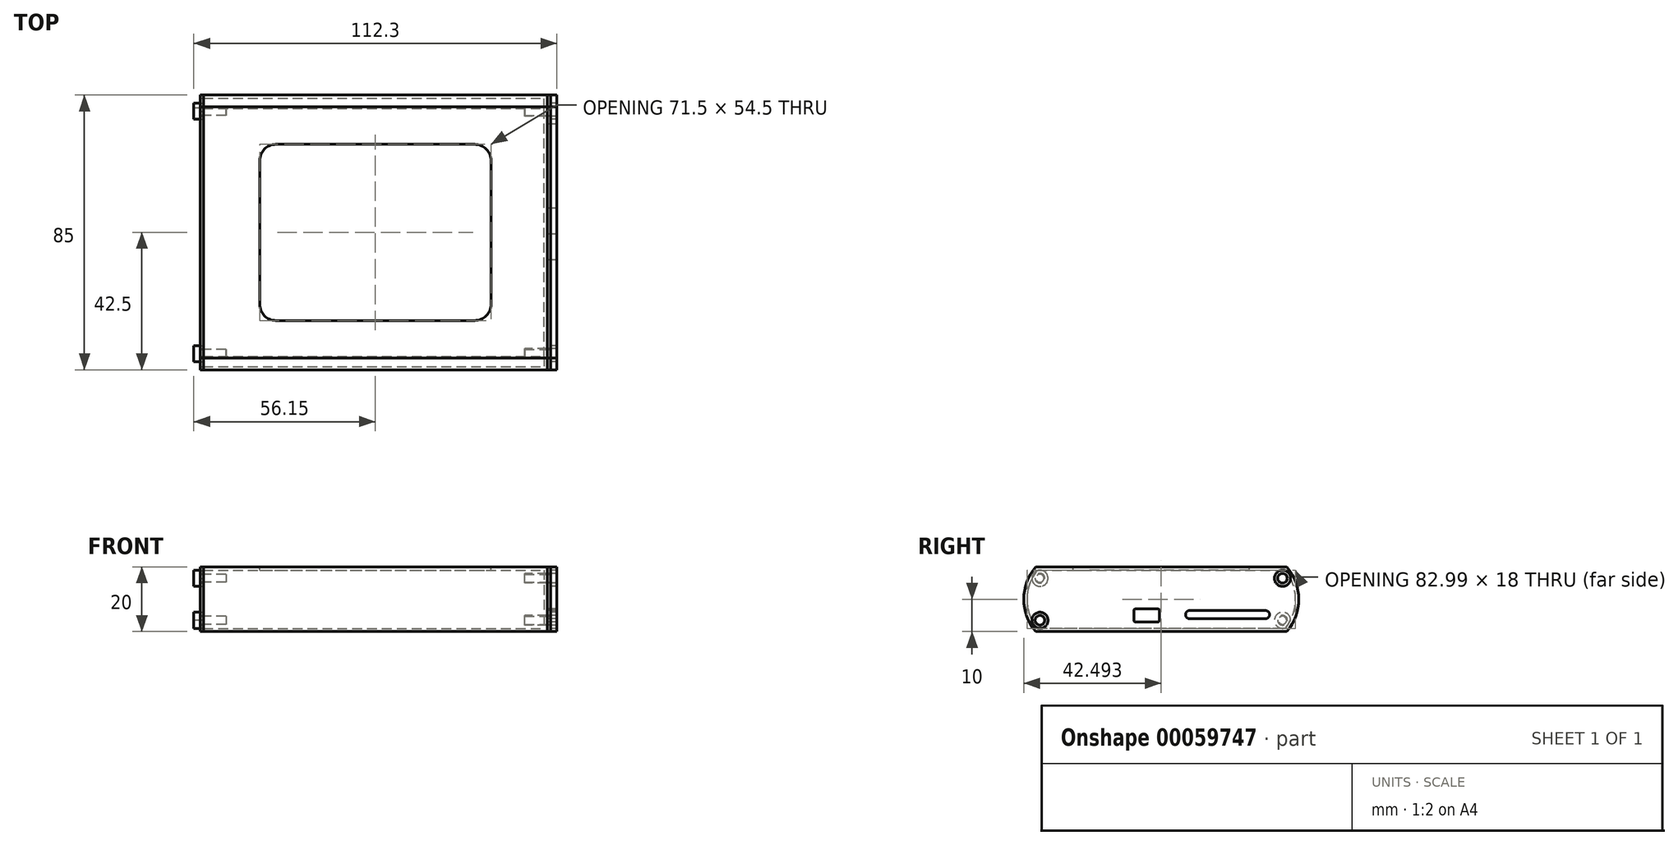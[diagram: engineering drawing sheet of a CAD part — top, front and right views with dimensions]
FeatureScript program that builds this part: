
annotation { "Feature Type Name" : "Feature", "Feature Type Description" : "" }
export const myFeature = defineFeature(function(context is Context, id is Id, definition is map)
    precondition{}
    {
        {
            var Q0;
            Q0=qCreatedBy(makeId("Right.planeOp"),FACE);
            var sketch = newSketch(context, id + "F0", { "sketchPlane" : qUnion([Q0])});
            skLineSegment(sketch, "E0", {"start": v(0, 24.02) * mm, "end": v(0, -24.32) * mm, "construction": true});
            skLineSegment(sketch, "E1", {"start": v(-38.85, 21.54) * mm, "end": v(-38.85, -24.6) * mm, "construction": true});
            skLineSegment(sketch, "E2", {"start": v(-42.5, 19.5) * mm, "end": v(-42.5, -17.74) * mm, "construction": true});
            skLineSegment(sketch, "E3.MirrorCS", {"start": v(38.85, 21.54) * mm, "end": v(38.85, -24.6) * mm, "construction": true});
            skLineSegment(sketch, "E4.MirrorCS", {"start": v(42.5, 19.5) * mm, "end": v(42.5, -17.74) * mm, "construction": true});
            skLineSegment(sketch, "E5", {"start": v(-46.74, 0) * mm, "end": v(47.17, 0) * mm, "construction": true});
            skLineSegment(sketch, "E6", {"start": v(0, 10) * mm, "end": v(-38.85, 10) * mm});
            skLineSegment(sketch, "E7.MirrorCS", {"start": v(0, -10) * mm, "end": v(-38.85, -10) * mm});
            skLineSegment(sketch, "E8.MirrorCS", {"start": v(0, 10) * mm, "end": v(38.85, 10) * mm});
            skLineSegment(sketch, "E9.MirrorCS", {"start": v(0, -10) * mm, "end": v(38.85, -10) * mm});
            skArc(sketch, "E10", {"start": v(-38.85, 10) * mm, "mid": v(-42.5, 0) * mm, "end": v(-38.85, -10) * mm});
            skArc(sketch, "E11.MirrorCS", {"start": v(38.85, 10) * mm, "mid": v(42.5, 0) * mm, "end": v(38.85, -10) * mm});
            skPoint(sketch, "E12.end.orphan", {"position": v(-42.5, 0) * mm});
            skPoint(sketch, "E12.start.orphan", {"position": v(-42.5, 10) * mm});
            skPoint(sketch, "E13.orphan", {"position": v(-42.5, -10) * mm});
            skPoint(sketch, "E14.MirrorCS.end.orphan", {"position": v(42.5, 0) * mm});
            skPoint(sketch, "E14.MirrorCS.start.orphan", {"position": v(42.5, 10) * mm});
            skPoint(sketch, "E15.MirrorCS.start.orphan", {"position": v(42.5, -10) * mm});
            skLineSegment(sketch, "E16", {"start": v(-37.5, 21.54) * mm, "end": v(-37.5, -22.5) * mm, "construction": true});
            skLineSegment(sketch, "E17.MirrorCS", {"start": v(37.5, 21.54) * mm, "end": v(37.5, -22.5) * mm, "construction": true});
            skLineSegment(sketch, "E18", {"start": v(-46, 6.5) * mm, "end": v(47.32, 6.5) * mm, "construction": true});
            skLineSegment(sketch, "E19.MirrorCS", {"start": v(-46, -6.5) * mm, "end": v(47.32, -6.5) * mm, "construction": true});
            skCircle(sketch, "E20", {"center": v(-37.5, 6.5) * mm, "radius": 1.5 * mm});
            skCircle(sketch, "E21.MirrorC", {"center": v(-37.5, -6.5) * mm, "radius": 1.5 * mm});
            skCircle(sketch, "E22.MirrorC", {"center": v(37.5, 6.5) * mm, "radius": 1.5 * mm});
            skCircle(sketch, "E23.MirrorC", {"center": v(37.5, -6.5) * mm, "radius": 1.5 * mm});
            skLineSegment(sketch, "E24", {"start": v(-8.5, 1.78) * mm, "end": v(-8.5, -12.6) * mm, "construction": true});
            skLineSegment(sketch, "E25", {"start": v(-0.5, 1.78) * mm, "end": v(-0.5, -12.5) * mm, "construction": true});
            skLineSegment(sketch, "E26", {"start": v(-11.94, -7) * mm, "end": v(1.3, -7) * mm, "construction": true});
            skLineSegment(sketch, "E27", {"start": v(-11.82, -3) * mm, "end": v(1.98, -3) * mm, "construction": true});
            skLineSegment(sketch, "E28.bottom", {"start": v(-8, -3) * mm, "end": v(-1, -3) * mm});
            skLineSegment(sketch, "E28.top", {"start": v(-8, -7) * mm, "end": v(-1, -7) * mm});
            skLineSegment(sketch, "E28.left", {"start": v(-8.5, -3.5) * mm, "end": v(-8.5, -6.5) * mm});
            skLineSegment(sketch, "E28.right", {"start": v(-0.5, -3.5) * mm, "end": v(-0.5, -6.5) * mm});
            skPoint(sketch, "E29.visualSharp", {"position": v(-8.5, -3) * mm});
            skArc(sketch, "E29.filletArc", {"start": v(-8, -3) * mm, "mid": v(-8.35, -3.15) * mm, "end": v(-8.5, -3.5) * mm});
            skPoint(sketch, "E30.visualSharp", {"position": v(-0.5, -3) * mm});
            skArc(sketch, "E30.filletArc", {"start": v(-0.5, -3.5) * mm, "mid": v(-0.65, -3.15) * mm, "end": v(-1, -3) * mm});
            skPoint(sketch, "E31.visualSharp", {"position": v(-8.5, -7) * mm});
            skArc(sketch, "E31.filletArc", {"start": v(-8.5, -6.5) * mm, "mid": v(-8.35, -6.85) * mm, "end": v(-8, -7) * mm});
            skPoint(sketch, "E32.visualSharp", {"position": v(-0.5, -7) * mm});
            skArc(sketch, "E32.filletArc", {"start": v(-1, -7) * mm, "mid": v(-0.65, -6.85) * mm, "end": v(-0.5, -6.5) * mm});
            skLineSegment(sketch, "E33", {"start": v(2.96, -6) * mm, "end": v(35.29, -6) * mm, "construction": true});
            skLineSegment(sketch, "E34", {"start": v(2.79, -3.5) * mm, "end": v(35.16, -3.5) * mm, "construction": true});
            skLineSegment(sketch, "E35", {"start": v(7.5, -2.13) * mm, "end": v(7.5, -7.86) * mm, "construction": true});
            skLineSegment(sketch, "E36", {"start": v(33.5, -2.56) * mm, "end": v(33.5, -7.05) * mm, "construction": true});
            skLineSegment(sketch, "E37", {"start": v(5.6, -4.75) * mm, "end": v(35.16, -4.75) * mm, "construction": true});
            skLineSegment(sketch, "E38.bottom", {"start": v(8.75, -3.5) * mm, "end": v(32.25, -3.5) * mm});
            skLineSegment(sketch, "E38.top", {"start": v(8.75, -6) * mm, "end": v(32.25, -6) * mm});
            skLineSegment(sketch, "E39", {"start": v(8.75, -2.05) * mm, "end": v(8.75, -8.42) * mm, "construction": true});
            skLineSegment(sketch, "E40", {"start": v(32.25, -2.56) * mm, "end": v(32.25, -7.3) * mm, "construction": true});
            skArc(sketch, "E41", {"start": v(8.75, -3.5) * mm, "mid": v(7.5, -4.75) * mm, "end": v(8.75, -6) * mm});
            skArc(sketch, "E42", {"start": v(32.25, -6) * mm, "mid": v(33.5, -4.75) * mm, "end": v(32.25, -3.5) * mm});
            skSolve(sketch);
        }
        {
            var Q0;
            Q0=makeQuery(id+"F0.imprint","IMPRINT",FACE,{"disambiguationData":[TD([[makeQuery(id+"F0.imprint","IMPRINT",EDGE,{"derivedFrom":sQuery(id+"F0.wireOp",EDGE,"E6")}),1.0]])]});
            extrude(context, id + "F1", {"entities" : qUnion([Q0]), "depth" : 1 * mm});
        }
        {
            var Q0;
            Q0=makeQuery(id+"F1.opExtrude","CAP_FACE",FACE,{"disambiguationData":[OSD([sQuery(id+"F0.wireOp",EDGE,"E6"),sQuery(id+"F0.wireOp",EDGE,"E7.MirrorCS"),sQuery(id+"F0.wireOp",EDGE,"E8.MirrorCS"),sQuery(id+"F0.wireOp",EDGE,"E9.MirrorCS"),sQuery(id+"F0.wireOp",EDGE,"E10"),sQuery(id+"F0.wireOp",EDGE,"E11.MirrorCS"),sQuery(id+"F0.wireOp",EDGE,"E20"),sQuery(id+"F0.wireOp",EDGE,"E21.MirrorC"),sQuery(id+"F0.wireOp",EDGE,"E22.MirrorC"),sQuery(id+"F0.wireOp",EDGE,"E23.MirrorC"),sQuery(id+"F0.wireOp",EDGE,"E28.bottom"),sQuery(id+"F0.wireOp",EDGE,"E28.top"),sQuery(id+"F0.wireOp",EDGE,"E28.left"),sQuery(id+"F0.wireOp",EDGE,"E28.right"),sQuery(id+"F0.wireOp",EDGE,"E29.filletArc"),sQuery(id+"F0.wireOp",EDGE,"E30.filletArc"),sQuery(id+"F0.wireOp",EDGE,"E31.filletArc"),sQuery(id+"F0.wireOp",EDGE,"E32.filletArc"),sQuery(id+"F0.wireOp",EDGE,"E38.bottom"),sQuery(id+"F0.wireOp",EDGE,"E38.top"),sQuery(id+"F0.wireOp",EDGE,"E41"),sQuery(id+"F0.wireOp",EDGE,"E42")])],"isStart":false});
            var sketch = newSketch(context, id + "F2", { "sketchPlane" : qUnion([Q0])});
            skCircle(sketch, "E43", {"center": v(-37.5, 6.5) * mm, "radius": 2.5 * mm});
            skCircle(sketch, "E44", {"center": v(-37.5, 6.5) * mm, "radius": 1.25 * mm});
            skCircle(sketch, "E45.MirrorC", {"center": v(37.5, 6.5) * mm, "radius": 2.5 * mm});
            skCircle(sketch, "E46.MirrorC", {"center": v(37.5, 6.5) * mm, "radius": 1.25 * mm});
            skCircle(sketch, "E47.MirrorC", {"center": v(-37.5, -6.5) * mm, "radius": 2.5 * mm});
            skCircle(sketch, "E48.MirrorC", {"center": v(-37.5, -6.5) * mm, "radius": 1.25 * mm});
            skCircle(sketch, "E49.MirrorC", {"center": v(37.5, -6.5) * mm, "radius": 1.25 * mm});
            skCircle(sketch, "E50.MirrorC", {"center": v(37.5, -6.5) * mm, "radius": 2.5 * mm});
            skSolve(sketch);
        }
        {
            var Q0;
            Q0=makeQuery(id+"F2.imprint","IMPRINT",FACE,{"disambiguationData":[TD([[makeQuery(id+"F2.imprint","IMPRINT",EDGE,{"derivedFrom":sQuery(id+"F2.wireOp",EDGE,"E44")}),-1.0]])]});
            var Q1;
            Q1=makeQuery(id+"F2.imprint","IMPRINT",FACE,{"disambiguationData":[TD([[makeQuery(id+"F2.imprint","IMPRINT",EDGE,{"derivedFrom":sQuery(id+"F2.wireOp",EDGE,"E44")}),1.0]])]});
            var Q2;
            Q2=makeQuery(id+"F2.imprint","IMPRINT",FACE,{"disambiguationData":[TD([[makeQuery(id+"F2.imprint","IMPRINT",EDGE,{"derivedFrom":sQuery(id+"F2.wireOp",EDGE,"E43")}),1.0]])]});
            var Q3;
            Q3=makeQuery(id+"F2.imprint","IMPRINT",FACE,{"disambiguationData":[TD([[makeQuery(id+"F2.imprint","IMPRINT",EDGE,{"derivedFrom":sQuery(id+"F2.wireOp",EDGE,"E45.MirrorC")}),-1.0]])]});
            var Q4;
            Q4=makeQuery(id+"F2.imprint","IMPRINT",FACE,{"disambiguationData":[TD([[makeQuery(id+"F2.imprint","IMPRINT",EDGE,{"derivedFrom":sQuery(id+"F2.wireOp",EDGE,"E46.MirrorC")}),-1.0]])]});
            var Q5;
            Q5=makeQuery(id+"F2.imprint","IMPRINT",FACE,{"disambiguationData":[TD([[makeQuery(id+"F2.imprint","IMPRINT",EDGE,{"derivedFrom":sQuery(id+"F2.wireOp",EDGE,"E46.MirrorC")}),1.0]])]});
            var Q6;
            Q6=makeQuery(id+"F2.imprint","IMPRINT",FACE,{"disambiguationData":[TD([[makeQuery(id+"F2.imprint","IMPRINT",EDGE,{"derivedFrom":sQuery(id+"F2.wireOp",EDGE,"E49.MirrorC")}),1.0]])]});
            var Q7;
            Q7=makeQuery(id+"F2.imprint","IMPRINT",FACE,{"disambiguationData":[TD([[makeQuery(id+"F2.imprint","IMPRINT",EDGE,{"derivedFrom":sQuery(id+"F2.wireOp",EDGE,"E49.MirrorC")}),-1.0]])]});
            var Q8;
            Q8=makeQuery(id+"F2.imprint","IMPRINT",FACE,{"disambiguationData":[TD([[makeQuery(id+"F2.imprint","IMPRINT",EDGE,{"derivedFrom":sQuery(id+"F2.wireOp",EDGE,"E50.MirrorC")}),1.0]])]});
            var Q9;
            Q9=makeQuery(id+"F2.imprint","IMPRINT",FACE,{"disambiguationData":[TD([[makeQuery(id+"F2.imprint","IMPRINT",EDGE,{"derivedFrom":sQuery(id+"F2.wireOp",EDGE,"E48.MirrorC")}),-1.0]])]});
            var Q10;
            Q10=makeQuery(id+"F2.imprint","IMPRINT",FACE,{"disambiguationData":[TD([[makeQuery(id+"F2.imprint","IMPRINT",EDGE,{"derivedFrom":sQuery(id+"F2.wireOp",EDGE,"E48.MirrorC")}),1.0]])]});
            var Q11;
            Q11=makeQuery(id+"F2.imprint","IMPRINT",FACE,{"disambiguationData":[TD([[makeQuery(id+"F2.imprint","IMPRINT",EDGE,{"derivedFrom":sQuery(id+"F2.wireOp",EDGE,"E47.MirrorC")}),-1.0]])]});
            extrude(context, id + "F3", {"entities" : qUnion([Q0, Q1, Q2, Q3, Q4, Q5, Q6, Q7, Q8, Q9, Q10, Q11]), "depth" : 2 * mm});
        }
        {
            var Q0;
            Q0=makeQuery(id+"F2.imprint","IMPRINT",FACE,{"disambiguationData":[TD([[makeQuery(id+"F2.imprint","IMPRINT",EDGE,{"derivedFrom":sQuery(id+"F2.wireOp",EDGE,"E44")}),1.0]])]});
            var Q1;
            Q1=makeQuery(id+"F2.imprint","IMPRINT",FACE,{"disambiguationData":[TD([[makeQuery(id+"F2.imprint","IMPRINT",EDGE,{"derivedFrom":sQuery(id+"F2.wireOp",EDGE,"E48.MirrorC")}),-1.0]])]});
            var Q2;
            Q2=makeQuery(id+"F2.imprint","IMPRINT",FACE,{"disambiguationData":[TD([[makeQuery(id+"F2.imprint","IMPRINT",EDGE,{"derivedFrom":sQuery(id+"F2.wireOp",EDGE,"E46.MirrorC")}),-1.0]])]});
            var Q3;
            Q3=makeQuery(id+"F2.imprint","IMPRINT",FACE,{"disambiguationData":[TD([[makeQuery(id+"F2.imprint","IMPRINT",EDGE,{"derivedFrom":sQuery(id+"F2.wireOp",EDGE,"E49.MirrorC")}),1.0]])]});
            extrude(context, id + "F4", {"entities" : qUnion([Q0, Q1, Q2, Q3]), "operationType" : NewBodyOperationType.ADD, "oppositeDirection" : true, "depth" : 8 * mm});
        }
        {
            var Q0;
            Q0=makeQuery(id+"F0.imprint","IMPRINT",FACE,{"disambiguationData":[TD([[makeQuery(id+"F0.imprint","IMPRINT",EDGE,{"derivedFrom":sQuery(id+"F0.wireOp",EDGE,"E6")}),1.0]])]});
            var sketch = newSketch(context, id + "F5", { "sketchPlane" : qUnion([Q0])});
            skLineSegment(sketch, "E51.0", {"start": v(0, 10) * mm, "end": v(-38.85, 10) * mm});
            skArc(sketch, "E51.1", {"start": v(-38.85, 10) * mm, "mid": v(-42.5, 0) * mm, "end": v(-38.85, -10) * mm});
            skLineSegment(sketch, "E51.2", {"start": v(0, -10) * mm, "end": v(-38.85, -10) * mm});
            skLineSegment(sketch, "E51.3", {"start": v(0, -10) * mm, "end": v(38.85, -10) * mm});
            skLineSegment(sketch, "E51.4", {"start": v(0, 10) * mm, "end": v(38.85, 10) * mm});
            skArc(sketch, "E51.5", {"start": v(38.85, 10) * mm, "mid": v(42.5, 0) * mm, "end": v(38.85, -10) * mm});
            skSolve(sketch);
        }
        {
            var Q0;
            Q0 = qSketchRegion(id + "F5", true);
            extrude(context, id + "F6", {"entities" : qUnion([Q0]), "oppositeDirection" : true, "depth" : 106.3 * mm});
        }
        {
            var Q0;
            Q0=makeQuery(id+"F6.opExtrude","CAP_FACE",FACE,{"disambiguationData":[OSD([sQuery(id+"F5.wireOp",EDGE,"E51.0"),sQuery(id+"F5.wireOp",EDGE,"E51.1"),sQuery(id+"F5.wireOp",EDGE,"E51.2"),sQuery(id+"F5.wireOp",EDGE,"E51.3"),sQuery(id+"F5.wireOp",EDGE,"E51.4"),sQuery(id+"F5.wireOp",EDGE,"E51.5")])],"isStart":false});
            shell(context, id + "F7", {"entities" : qUnion([Q0]), "thickness" : 1 * mm});
        }
        {
            var Q0;
            Q0=makeQuery(id+"F6.opExtrude","SWEPT_FACE",FACE,{"disambiguationData":[OSD([sQuery(id+"F5.wireOp",EDGE,"E51.0"),sQuery(id+"F5.wireOp",EDGE,"E51.4")])]});
            var sketch = newSketch(context, id + "F8", { "sketchPlane" : qUnion([Q0])});
            skLineSegment(sketch, "E52.0", {"start": v(-106.3, 38.85) * mm, "end": v(0, 38.85) * mm});
            skLineSegment(sketch, "E53.0", {"start": v(-106.3, -38.85) * mm, "end": v(-106.3, 38.85) * mm});
            skLineSegment(sketch, "E54.0", {"start": v(-106.3, -38.85) * mm, "end": v(0, -38.85) * mm});
            skLineSegment(sketch, "E55.0", {"start": v(0, -38.85) * mm, "end": v(0, 38.85) * mm});
            skLineSegment(sketch, "E56", {"start": v(-53.15, 38.85) * mm, "end": v(-53.15, -38.85) * mm, "construction": true});
            skLineSegment(sketch, "E57", {"start": v(-106.3, 0) * mm, "end": v(0.85, 0) * mm, "construction": true});
            skPoint(sketch, "E57.endSnap0", {"position": v(0, 0) * mm});
            skLineSegment(sketch, "E58", {"start": v(-92, 38.85) * mm, "end": v(-92, -38.85) * mm, "construction": true});
            skLineSegment(sketch, "E59", {"start": v(-106.3, 30) * mm, "end": v(0, 30) * mm, "construction": true});
            skLineSegment(sketch, "E60.MirrorCS", {"start": v(-106.3, -30) * mm, "end": v(0, -30) * mm, "construction": true});
            skLineSegment(sketch, "E61.MirrorCS", {"start": v(-14.3, 38.85) * mm, "end": v(-14.3, -38.85) * mm, "construction": true});
            skLineSegment(sketch, "E62", {"start": v(-82, 30) * mm, "end": v(-53.15, 30) * mm});
            skLineSegment(sketch, "E63", {"start": v(-92, 20) * mm, "end": v(-92, 0) * mm});
            skLineSegment(sketch, "E64.MirrorCS", {"start": v(-82, -30) * mm, "end": v(-53.15, -30) * mm});
            skLineSegment(sketch, "E65.MirrorCS", {"start": v(-92, -20) * mm, "end": v(-92, 0) * mm});
            skLineSegment(sketch, "E66.MirrorCS", {"start": v(-24.3, 30) * mm, "end": v(-53.15, 30) * mm});
            skLineSegment(sketch, "E67.MirrorCS", {"start": v(-14.3, 20) * mm, "end": v(-14.3, 0) * mm});
            skLineSegment(sketch, "E68.MirrorCS", {"start": v(-14.3, -20) * mm, "end": v(-14.3, 0) * mm});
            skLineSegment(sketch, "E69.MirrorCS", {"start": v(-24.3, -30) * mm, "end": v(-53.15, -30) * mm});
            skPoint(sketch, "E70.visualSharp", {"position": v(-92, 30) * mm});
            skArc(sketch, "E70.filletArc", {"start": v(-82, 30) * mm, "mid": v(-89.07, 27.07) * mm, "end": v(-92, 20) * mm});
            skPoint(sketch, "E71.visualSharp", {"position": v(-14.3, 30) * mm});
            skArc(sketch, "E71.filletArc", {"start": v(-14.3, 20) * mm, "mid": v(-17.23, 27.07) * mm, "end": v(-24.3, 30) * mm});
            skPoint(sketch, "E72.visualSharp", {"position": v(-14.3, -30) * mm});
            skArc(sketch, "E72.filletArc", {"start": v(-24.3, -30) * mm, "mid": v(-17.23, -27.07) * mm, "end": v(-14.3, -20) * mm});
            skPoint(sketch, "E73.visualSharp", {"position": v(-92, -30) * mm});
            skArc(sketch, "E73.filletArc", {"start": v(-92, -20) * mm, "mid": v(-89.07, -27.07) * mm, "end": v(-82, -30) * mm});
            skLineSegment(sketch, "E74", {"start": v(-88.9, 36.04) * mm, "end": v(-88.9, -35.35) * mm, "construction": true});
            skLineSegment(sketch, "E75", {"start": v(-95.18, 27.25) * mm, "end": v(-10.45, 27.25) * mm, "construction": true});
            skLineSegment(sketch, "E76.MirrorCS", {"start": v(-95.18, -27.25) * mm, "end": v(-10.45, -27.25) * mm, "construction": true});
            skLineSegment(sketch, "E77.MirrorCS", {"start": v(-88.9, -36.04) * mm, "end": v(-88.9, 35.35) * mm, "construction": true});
            skLineSegment(sketch, "E78.MirrorCS", {"start": v(-17.4, 36.04) * mm, "end": v(-17.4, -35.35) * mm, "construction": true});
            skLineSegment(sketch, "E79.bottom", {"start": v(-83.9, 27.25) * mm, "end": v(-22.4, 27.25) * mm});
            skLineSegment(sketch, "E79.top", {"start": v(-83.9, -27.25) * mm, "end": v(-22.4, -27.25) * mm});
            skLineSegment(sketch, "E79.left", {"start": v(-88.9, 22.25) * mm, "end": v(-88.9, -22.25) * mm});
            skLineSegment(sketch, "E79.right", {"start": v(-17.4, 22.25) * mm, "end": v(-17.4, -22.25) * mm});
            skPoint(sketch, "E80.visualSharp", {"position": v(-88.9, 27.25) * mm});
            skArc(sketch, "E80.filletArc", {"start": v(-83.9, 27.25) * mm, "mid": v(-87.44, 25.79) * mm, "end": v(-88.9, 22.25) * mm});
            skPoint(sketch, "E81.visualSharp", {"position": v(-17.4, 27.25) * mm});
            skArc(sketch, "E81.filletArc", {"start": v(-17.4, 22.25) * mm, "mid": v(-18.86, 25.79) * mm, "end": v(-22.4, 27.25) * mm});
            skPoint(sketch, "E82.visualSharp", {"position": v(-17.4, -27.25) * mm});
            skArc(sketch, "E82.filletArc", {"start": v(-22.4, -27.25) * mm, "mid": v(-18.86, -25.79) * mm, "end": v(-17.4, -22.25) * mm});
            skPoint(sketch, "E83.visualSharp", {"position": v(-88.9, -27.25) * mm});
            skArc(sketch, "E83.filletArc", {"start": v(-88.9, -22.25) * mm, "mid": v(-87.44, -25.79) * mm, "end": v(-83.9, -27.25) * mm});
            skSolve(sketch);
        }
        {
            var Q0;
            Q0=makeQuery(id+"F8.imprint","IMPRINT",FACE,{"disambiguationData":[TD([[makeQuery(id+"F8.imprint","IMPRINT",EDGE,{"derivedFrom":sQuery(id+"F8.wireOp",EDGE,"E79.bottom")}),-1.0]])]});
            var Q1;
            Q1=makeQuery(id+"F7.opShell","OFFSET_FACE",FACE,{"disambiguationData":[OSD([sQuery(id+"F5.wireOp",EDGE,"E51.0"),sQuery(id+"F5.wireOp",EDGE,"E51.4")])]});
            extrude(context, id + "F9", {"entities" : qUnion([Q0]), "operationType" : NewBodyOperationType.REMOVE, "endBound" : BoundingType.UP_TO_SURFACE, "oppositeDirection" : true, "endBoundEntityFace" : qUnion([Q1]), "depth" : 25 * mm});
        }
        {
            var Q0;
            Q0=makeQuery(id+"F6.opExtrude","CAP_FACE",FACE,{"disambiguationData":[OSD([sQuery(id+"F5.wireOp",EDGE,"E51.0"),sQuery(id+"F5.wireOp",EDGE,"E51.1"),sQuery(id+"F5.wireOp",EDGE,"E51.2"),sQuery(id+"F5.wireOp",EDGE,"E51.3"),sQuery(id+"F5.wireOp",EDGE,"E51.4"),sQuery(id+"F5.wireOp",EDGE,"E51.5")])],"isStart":false});
            var sketch = newSketch(context, id + "F10", { "sketchPlane" : qUnion([Q0])});
            skLineSegment(sketch, "E84.0", {"start": v(0, 10) * mm, "end": v(-38.85, 10) * mm});
            skArc(sketch, "E85.0", {"start": v(-38.85, 10) * mm, "mid": v(-42.5, 0) * mm, "end": v(-38.85, -10) * mm});
            skLineSegment(sketch, "E86.0", {"start": v(0, -10) * mm, "end": v(-38.85, -10) * mm});
            skLineSegment(sketch, "E87.0", {"start": v(0, -10) * mm, "end": v(38.85, -10) * mm});
            skLineSegment(sketch, "E88.0", {"start": v(0, 10) * mm, "end": v(38.85, 10) * mm});
            skArc(sketch, "E89.0", {"start": v(38.85, 10) * mm, "mid": v(42.5, 0) * mm, "end": v(38.85, -10) * mm});
            skCircle(sketch, "E90.0", {"center": v(-37.5, 6.5) * mm, "radius": 1.5 * mm});
            skCircle(sketch, "E91.0", {"center": v(-37.5, -6.5) * mm, "radius": 1.5 * mm});
            skCircle(sketch, "E92.0", {"center": v(37.5, 6.5) * mm, "radius": 1.5 * mm});
            skCircle(sketch, "E93.0", {"center": v(37.5, -6.5) * mm, "radius": 1.5 * mm});
            skCircle(sketch, "E94.0", {"center": v(-37.5, 6.5) * mm, "radius": 1.25 * mm});
            skCircle(sketch, "E95.0.0", {"center": v(-37.5, -6.5) * mm, "radius": 1.25 * mm});
            skCircle(sketch, "E96.0", {"center": v(37.5, 6.5) * mm, "radius": 1.25 * mm});
            skCircle(sketch, "E97.0", {"center": v(37.5, -6.5) * mm, "radius": 1.25 * mm});
            skLineSegment(sketch, "E98.0.0", {"start": v(38.85, 10) * mm, "end": v(-38.85, 10) * mm});
            skLineSegment(sketch, "E98.0.2", {"start": v(-38.85, -10) * mm, "end": v(38.85, -10) * mm});
            skArc(sketch, "E98.0.3", {"start": v(38.85, -10) * mm, "mid": v(42.5, 0) * mm, "end": v(38.85, 10) * mm});
            skCircle(sketch, "E99.0.0", {"center": v(-37.5, 6.5) * mm, "radius": 2.5 * mm});
            skCircle(sketch, "E100.0", {"center": v(-37.5, -6.5) * mm, "radius": 2.5 * mm});
            skCircle(sketch, "E101.0", {"center": v(37.5, 6.5) * mm, "radius": 2.5 * mm});
            skCircle(sketch, "E102.0", {"center": v(37.5, -6.5) * mm, "radius": 2.5 * mm});
            skSolve(sketch);
        }
        {
            var Q0;
            {var subQ0=sQuery(id+"F10.wireOp",EDGE,"E99.0.0");var subQ1=sQuery(id+"F5.wireOp",EDGE,"E51.5");var subQ2=makeQuery(id+"F7.opShell","OFFSET_EDGE",EDGE,{"disambiguationData":[OSD([subQ1]),TDD([makeQuery(id+"F6.opExtrude","CAP_EDGE",EDGE,{"disambiguationData":[OSD([subQ1])],"isStart":false})])]});var subQ3=makeQuery(id+"F10.imprint","INTERSECT",VERTEX,{"disambiguationData":[OD(0.0)],"derivedFrom":[subQ2,subQ0]});Q0=makeQuery(id+"F10.imprint","IMPRINT",FACE,{"disambiguationData":[TD([[makeQuery(id+"F10.imprint","IMPRINT",EDGE,{"disambiguationData":[TD([[subQ3,1.0]])],"derivedFrom":subQ0}),-1.0]])]});}
            var Q1;
            {var subQ0=sQuery(id+"F10.wireOp",EDGE,"E100.0");var subQ1=sQuery(id+"F5.wireOp",EDGE,"E51.5");var subQ2=makeQuery(id+"F7.opShell","OFFSET_EDGE",EDGE,{"disambiguationData":[OSD([subQ1]),TDD([makeQuery(id+"F6.opExtrude","CAP_EDGE",EDGE,{"disambiguationData":[OSD([subQ1])],"isStart":false})])]});var subQ3=makeQuery(id+"F10.imprint","INTERSECT",VERTEX,{"disambiguationData":[OD(0.0)],"derivedFrom":[subQ2,subQ0]});Q1=makeQuery(id+"F10.imprint","IMPRINT",FACE,{"disambiguationData":[TD([[makeQuery(id+"F10.imprint","IMPRINT",EDGE,{"disambiguationData":[TD([[subQ3,-1.0]])],"derivedFrom":subQ0}),-1.0]])]});}
            var Q2;
            {var subQ0=sQuery(id+"F10.wireOp",EDGE,"E101.0");var subQ5=sQuery(id+"F5.wireOp",EDGE,"E51.1");var subQ6=makeQuery(id+"F7.opShell","OFFSET_EDGE",EDGE,{"disambiguationData":[OSD([subQ5]),TDD([makeQuery(id+"F6.opExtrude","CAP_EDGE",EDGE,{"disambiguationData":[OSD([subQ5])],"isStart":false})])]});var subQ7=makeQuery(id+"F10.imprint","INTERSECT",VERTEX,{"disambiguationData":[OD(0.0)],"derivedFrom":[subQ6,subQ0]});Q2=makeQuery(id+"F10.imprint","IMPRINT",FACE,{"disambiguationData":[TD([[makeQuery(id+"F10.imprint","IMPRINT",EDGE,{"disambiguationData":[TD([[subQ7,-1.0]])],"derivedFrom":subQ0}),-1.0]])]});}
            var Q3;
            {var subQ0=sQuery(id+"F10.wireOp",EDGE,"E102.0");var subQ5=sQuery(id+"F5.wireOp",EDGE,"E51.1");var subQ6=makeQuery(id+"F7.opShell","OFFSET_EDGE",EDGE,{"disambiguationData":[OSD([subQ5]),TDD([makeQuery(id+"F6.opExtrude","CAP_EDGE",EDGE,{"disambiguationData":[OSD([subQ5])],"isStart":false})])]});var subQ7=makeQuery(id+"F10.imprint","INTERSECT",VERTEX,{"disambiguationData":[OD(1.0)],"derivedFrom":[subQ6,subQ0]});Q3=makeQuery(id+"F10.imprint","IMPRINT",FACE,{"disambiguationData":[TD([[makeQuery(id+"F10.imprint","IMPRINT",EDGE,{"disambiguationData":[TD([[subQ7,1.0]])],"derivedFrom":subQ0}),-1.0]])]});}
            var Q4;
            {var subQ5=sQuery(id+"F5.wireOp",EDGE,"E51.1");var subQ6=makeQuery(id+"F7.opShell","OFFSET_EDGE",EDGE,{"disambiguationData":[OSD([subQ5]),TDD([makeQuery(id+"F6.opExtrude","CAP_EDGE",EDGE,{"disambiguationData":[OSD([subQ5])],"isStart":false})])]});var subQ8=sQuery(id+"F10.wireOp",EDGE,"E101.0");var subQ9=makeQuery(id+"F10.imprint","INTERSECT",VERTEX,{"disambiguationData":[OD(1.0)],"derivedFrom":[subQ6,subQ8]});Q4=makeQuery(id+"F10.imprint","IMPRINT",FACE,{"disambiguationData":[TD([[makeQuery(id+"F10.imprint","IMPRINT",EDGE,{"disambiguationData":[TD([[subQ9,-1.0]])],"derivedFrom":subQ6}),-1.0]])]});}
            var Q5;
            {var subQ22=sQuery(id+"F10.wireOp",EDGE,"E85.0");Q5=makeQuery(id+"F10.imprint","IMPRINT",FACE,{"disambiguationData":[TD([[makeQuery(id+"F10.imprint","IMPRINT",EDGE,{"derivedFrom":subQ22}),1.0]])]});}
            var Q6;
            {var subQ0=sQuery(id+"F10.wireOp",EDGE,"E102.0");var subQ1=sQuery(id+"F5.wireOp",EDGE,"E51.1");var subQ2=makeQuery(id+"F7.opShell","OFFSET_EDGE",EDGE,{"disambiguationData":[OSD([subQ1]),TDD([makeQuery(id+"F6.opExtrude","CAP_EDGE",EDGE,{"disambiguationData":[OSD([subQ1])],"isStart":false})])]});var subQ3=makeQuery(id+"F10.imprint","INTERSECT",VERTEX,{"disambiguationData":[OD(0.0)],"derivedFrom":[subQ2,subQ0]});Q6=makeQuery(id+"F10.imprint","IMPRINT",FACE,{"disambiguationData":[TD([[makeQuery(id+"F10.imprint","IMPRINT",EDGE,{"disambiguationData":[TD([[subQ3,1.0]])],"derivedFrom":subQ0}),1.0]])]});}
            var Q7;
            Q7=makeQuery(id+"F10.imprint","IMPRINT",FACE,{"disambiguationData":[TD([[makeQuery(id+"F10.imprint","IMPRINT",EDGE,{"derivedFrom":sQuery(id+"F10.wireOp",EDGE,"E93.0")}),-1.0]])]});
            var Q8;
            {var subQ0=sQuery(id+"F10.wireOp",EDGE,"E101.0");var subQ1=sQuery(id+"F5.wireOp",EDGE,"E51.1");var subQ2=makeQuery(id+"F7.opShell","OFFSET_EDGE",EDGE,{"disambiguationData":[OSD([subQ1]),TDD([makeQuery(id+"F6.opExtrude","CAP_EDGE",EDGE,{"disambiguationData":[OSD([subQ1])],"isStart":false})])]});var subQ3=makeQuery(id+"F10.imprint","INTERSECT",VERTEX,{"disambiguationData":[OD(0.0)],"derivedFrom":[subQ2,subQ0]});Q8=makeQuery(id+"F10.imprint","IMPRINT",FACE,{"disambiguationData":[TD([[makeQuery(id+"F10.imprint","IMPRINT",EDGE,{"disambiguationData":[TD([[subQ3,1.0]])],"derivedFrom":subQ0}),1.0]])]});}
            var Q9;
            Q9=makeQuery(id+"F10.imprint","IMPRINT",FACE,{"disambiguationData":[TD([[makeQuery(id+"F10.imprint","IMPRINT",EDGE,{"derivedFrom":sQuery(id+"F10.wireOp",EDGE,"E92.0")}),1.0]])]});
            var Q10;
            {var subQ0=sQuery(id+"F10.wireOp",EDGE,"E100.0");var subQ1=sQuery(id+"F5.wireOp",EDGE,"E51.5");var subQ2=makeQuery(id+"F7.opShell","OFFSET_EDGE",EDGE,{"disambiguationData":[OSD([subQ1]),TDD([makeQuery(id+"F6.opExtrude","CAP_EDGE",EDGE,{"disambiguationData":[OSD([subQ1])],"isStart":false})])]});var subQ3=makeQuery(id+"F10.imprint","INTERSECT",VERTEX,{"disambiguationData":[OD(0.0)],"derivedFrom":[subQ2,subQ0]});Q10=makeQuery(id+"F10.imprint","IMPRINT",FACE,{"disambiguationData":[TD([[makeQuery(id+"F10.imprint","IMPRINT",EDGE,{"disambiguationData":[TD([[subQ3,1.0]])],"derivedFrom":subQ0}),1.0]])]});}
            var Q11;
            {var subQ0=sQuery(id+"F10.wireOp",EDGE,"E99.0.0");var subQ1=sQuery(id+"F5.wireOp",EDGE,"E51.5");var subQ2=makeQuery(id+"F7.opShell","OFFSET_EDGE",EDGE,{"disambiguationData":[OSD([subQ1]),TDD([makeQuery(id+"F6.opExtrude","CAP_EDGE",EDGE,{"disambiguationData":[OSD([subQ1])],"isStart":false})])]});var subQ3=makeQuery(id+"F10.imprint","INTERSECT",VERTEX,{"disambiguationData":[OD(0.0)],"derivedFrom":[subQ2,subQ0]});Q11=makeQuery(id+"F10.imprint","IMPRINT",FACE,{"disambiguationData":[TD([[makeQuery(id+"F10.imprint","IMPRINT",EDGE,{"disambiguationData":[TD([[subQ3,-1.0]])],"derivedFrom":subQ0}),1.0]])]});}
            var Q12;
            Q12=makeQuery(id+"F10.imprint","IMPRINT",FACE,{"disambiguationData":[TD([[makeQuery(id+"F10.imprint","IMPRINT",EDGE,{"derivedFrom":sQuery(id+"F10.wireOp",EDGE,"E90.0")}),-1.0]])]});
            var Q13;
            Q13=makeQuery(id+"F10.imprint","IMPRINT",FACE,{"disambiguationData":[TD([[makeQuery(id+"F10.imprint","IMPRINT",EDGE,{"derivedFrom":sQuery(id+"F10.wireOp",EDGE,"E91.0")}),1.0]])]});
            extrude(context, id + "F11", {"entities" : qUnion([Q0, Q1, Q2, Q3, Q4, Q5, Q6, Q7, Q8, Q9, Q10, Q11, Q12, Q13]), "depth" : 1 * mm});
        }
        {
            var Q0;
            Q0=makeQuery(id+"F11.opExtrude","CAP_FACE",FACE,{"disambiguationData":[OSD([sQuery(id+"F10.wireOp",EDGE,"E98.0.0"),sQuery(id+"F10.wireOp",EDGE,"E85.0"),sQuery(id+"F10.wireOp",EDGE,"E98.0.2"),sQuery(id+"F10.wireOp",EDGE,"E98.0.3"),sQuery(id+"F10.wireOp",EDGE,"E99.0.0"),sQuery(id+"F10.wireOp",EDGE,"E100.0"),sQuery(id+"F10.wireOp",EDGE,"E101.0"),sQuery(id+"F10.wireOp",EDGE,"E102.0")])],"isStart":false});
            var sketch = newSketch(context, id + "F12", { "sketchPlane" : qUnion([Q0])});
            skCircle(sketch, "E103.0", {"center": v(-37.5, 6.5) * mm, "radius": 1.25 * mm});
            skCircle(sketch, "E104.0", {"center": v(-37.5, -6.5) * mm, "radius": 1.25 * mm});
            skCircle(sketch, "E105.0", {"center": v(37.5, 6.5) * mm, "radius": 1.25 * mm});
            skCircle(sketch, "E106.0", {"center": v(37.5, -6.5) * mm, "radius": 1.25 * mm});
            skCircle(sketch, "E107.0", {"center": v(37.5, -6.5) * mm, "radius": 2.5 * mm});
            skCircle(sketch, "E108.0", {"center": v(-37.5, -6.5) * mm, "radius": 2.5 * mm});
            skCircle(sketch, "E109.0", {"center": v(-37.5, 6.5) * mm, "radius": 2.5 * mm});
            skCircle(sketch, "E110.0", {"center": v(37.5, 6.5) * mm, "radius": 2.5 * mm});
            skSolve(sketch);
        }
        {
            var Q0;
            Q0=makeQuery(id+"F12.imprint","IMPRINT",FACE,{"disambiguationData":[TD([[makeQuery(id+"F12.imprint","IMPRINT",EDGE,{"derivedFrom":sQuery(id+"F12.wireOp",EDGE,"E107.0")}),1.0]])]});
            var Q1;
            Q1=makeQuery(id+"F12.imprint","IMPRINT",FACE,{"disambiguationData":[TD([[makeQuery(id+"F12.imprint","IMPRINT",EDGE,{"derivedFrom":sQuery(id+"F12.wireOp",EDGE,"E106.0")}),-1.0]])]});
            var Q2;
            Q2=makeQuery(id+"F12.imprint","IMPRINT",FACE,{"disambiguationData":[TD([[makeQuery(id+"F12.imprint","IMPRINT",EDGE,{"derivedFrom":sQuery(id+"F12.wireOp",EDGE,"E106.0")}),1.0]])]});
            var Q3;
            Q3=makeQuery(id+"F12.imprint","IMPRINT",FACE,{"disambiguationData":[TD([[makeQuery(id+"F12.imprint","IMPRINT",EDGE,{"derivedFrom":sQuery(id+"F12.wireOp",EDGE,"E105.0")}),1.0]])]});
            var Q4;
            Q4=makeQuery(id+"F12.imprint","IMPRINT",FACE,{"disambiguationData":[TD([[makeQuery(id+"F12.imprint","IMPRINT",EDGE,{"derivedFrom":sQuery(id+"F12.wireOp",EDGE,"E105.0")}),-1.0]])]});
            var Q5;
            Q5=makeQuery(id+"F12.imprint","IMPRINT",FACE,{"disambiguationData":[TD([[makeQuery(id+"F12.imprint","IMPRINT",EDGE,{"derivedFrom":sQuery(id+"F12.wireOp",EDGE,"E110.0")}),1.0]])]});
            var Q6;
            Q6=makeQuery(id+"F12.imprint","IMPRINT",FACE,{"disambiguationData":[TD([[makeQuery(id+"F12.imprint","IMPRINT",EDGE,{"derivedFrom":sQuery(id+"F12.wireOp",EDGE,"E104.0")}),1.0]])]});
            var Q7;
            Q7=makeQuery(id+"F12.imprint","IMPRINT",FACE,{"disambiguationData":[TD([[makeQuery(id+"F12.imprint","IMPRINT",EDGE,{"derivedFrom":sQuery(id+"F12.wireOp",EDGE,"E104.0")}),-1.0]])]});
            var Q8;
            Q8=makeQuery(id+"F12.imprint","IMPRINT",FACE,{"disambiguationData":[TD([[makeQuery(id+"F12.imprint","IMPRINT",EDGE,{"derivedFrom":sQuery(id+"F12.wireOp",EDGE,"E108.0")}),1.0]])]});
            var Q9;
            Q9=makeQuery(id+"F12.imprint","IMPRINT",FACE,{"disambiguationData":[TD([[makeQuery(id+"F12.imprint","IMPRINT",EDGE,{"derivedFrom":sQuery(id+"F12.wireOp",EDGE,"E103.0")}),1.0]])]});
            var Q10;
            Q10=makeQuery(id+"F12.imprint","IMPRINT",FACE,{"disambiguationData":[TD([[makeQuery(id+"F12.imprint","IMPRINT",EDGE,{"derivedFrom":sQuery(id+"F12.wireOp",EDGE,"E103.0")}),-1.0]])]});
            var Q11;
            Q11=makeQuery(id+"F12.imprint","IMPRINT",FACE,{"disambiguationData":[TD([[makeQuery(id+"F12.imprint","IMPRINT",EDGE,{"derivedFrom":sQuery(id+"F12.wireOp",EDGE,"E109.0")}),1.0]])]});
            var Q12;
            Q12=sQuery(id+"F12.wireOp",EDGE,"E109.0");
            var Q13;
            Q13=sQuery(id+"F12.wireOp",EDGE,"E110.0");
            var Q14;
            Q14=sQuery(id+"F12.wireOp",EDGE,"E107.0");
            var Q15;
            Q15=sQuery(id+"F12.wireOp",EDGE,"E108.0");
            extrude(context, id + "F13", {"entities" : qUnion([Q0, Q1, Q2, Q3, Q4, Q5, Q6, Q7, Q8, Q9, Q10, Q11]), "surfaceEntities" : qUnion([Q12, Q13, Q14, Q15]), "depth" : 2 * mm});
        }
        {
            var Q0;
            Q0=makeQuery(id+"F12.imprint","IMPRINT",FACE,{"disambiguationData":[TD([[makeQuery(id+"F12.imprint","IMPRINT",EDGE,{"derivedFrom":sQuery(id+"F12.wireOp",EDGE,"E106.0")}),1.0]])]});
            var Q1;
            Q1=makeQuery(id+"F12.imprint","IMPRINT",FACE,{"disambiguationData":[TD([[makeQuery(id+"F12.imprint","IMPRINT",EDGE,{"derivedFrom":sQuery(id+"F12.wireOp",EDGE,"E105.0")}),1.0]])]});
            var Q2;
            Q2=makeQuery(id+"F12.imprint","IMPRINT",FACE,{"disambiguationData":[TD([[makeQuery(id+"F12.imprint","IMPRINT",EDGE,{"derivedFrom":sQuery(id+"F12.wireOp",EDGE,"E103.0")}),1.0]])]});
            var Q3;
            Q3=makeQuery(id+"F12.imprint","IMPRINT",FACE,{"disambiguationData":[TD([[makeQuery(id+"F12.imprint","IMPRINT",EDGE,{"derivedFrom":sQuery(id+"F12.wireOp",EDGE,"E104.0")}),1.0]])]});
            var Q4;
            Q4=sQuery(id+"F12.wireOp",EDGE,"E106.0");
            var Q5;
            Q5=sQuery(id+"F12.wireOp",EDGE,"E104.0");
            var Q6;
            Q6=sQuery(id+"F12.wireOp",EDGE,"E103.0");
            var Q7;
            Q7=sQuery(id+"F12.wireOp",EDGE,"E105.0");
            extrude(context, id + "F14", {"entities" : qUnion([Q0, Q1, Q2, Q3]), "surfaceEntities" : qUnion([Q4, Q5, Q6, Q7]), "oppositeDirection" : true, "depth" : 8 * mm});
        }
    });
